MODEL slx_65e6816acb3b
CONFIG AbsTol = auto
CONFIG EnableMultiTasking = off
CONFIG FixedStep = 0.00001
CONFIG InitFcn = T = 0.0001;
VBUS = 12;

Wc = 10;
Ws = 50;
CONFIG MaxStep = auto
CONFIG MinStep = auto
CONFIG RelTol = 1e-3
CONFIG SampleTimeConstraint = Unconstrained
CONFIG SolverName = FixedStepAuto
CONFIG StartTime = 0.0
CONFIG StopTime = 5
BLOCK [SubSystem] Anti_Park
BLOCK [Fcn] Anti_Park/Fcn
  Expr = cos(u[1])*u[2]-sin(u[1])*u[3]
BLOCK [Fcn] Anti_Park/Fcn1
  Expr = sin(u[1])*u[2]+cos(u[1])*u[3]
BLOCK [Mux] Anti_Park/Mux1
  DisplayOption = bar
  Inputs = 3
BLOCK [Outport] Anti_Park/Ualpha
BLOCK [Outport] Anti_Park/Ubeta
  Port = 2
BLOCK [Inport] Anti_Park/Vd
  Port = 2
BLOCK [Inport] Anti_Park/Vq
BLOCK [Inport] Anti_Park/angle
  Port = 3
BLOCK [SubSystem] BPF滤波器Wc
BLOCK [Outport] BPF滤波器Wc/Out
BLOCK [TransferFcn] BPF滤波器Wc/Transfer Fcn1
  Denominator = [1 sqrt(2)*Wc Wc^2]
  Numerator = [Wc^2]
BLOCK [Inport] BPF滤波器Wc/Wc
BLOCK [SubSystem] BPF滤波器Wc1
  NameLocation = top
BLOCK [Outport] BPF滤波器Wc1/Out
BLOCK [TransferFcn] BPF滤波器Wc1/Transfer Fcn1
  Denominator = [1 sqrt(2)*Wc Wc^2]
  Numerator = [Wc^2]
BLOCK [Inport] BPF滤波器Wc1/Wc
BLOCK [SubSystem] BPF滤波器Wc2
  NameLocation = top
BLOCK [Outport] BPF滤波器Wc2/Out
BLOCK [TransferFcn] BPF滤波器Wc2/Transfer Fcn1
  Denominator = [1 sqrt(2)*Wc Wc^2]
  Numerator = [Wc^2]
BLOCK [Inport] BPF滤波器Wc2/Wc
BLOCK [SubSystem] BPF滤波器Ws
  NameLocation = top
BLOCK [Outport] BPF滤波器Ws/Out
BLOCK [TransferFcn] BPF滤波器Ws/Transfer Fcn1
  Denominator = [1 sqrt(2)*Ws Ws^2]
  Numerator = [Ws^2]
BLOCK [Inport] BPF滤波器Ws/Ws
BLOCK [SubSystem] CLARKE
BLOCK [Inport] CLARKE/A
BLOCK [Outport] CLARKE/Alpha
BLOCK [Inport] CLARKE/B
  Port = 2
BLOCK [Outport] CLARKE/Beta
  Port = 2
BLOCK [Inport] CLARKE/C
  Port = 3
BLOCK [Mux] CLARKE/Mux
  DisplayOption = bar
  Inputs = 3
BLOCK [Fcn] CLARKE/alpha
  Expr = (u(1)-0.5*(u(2)+u(3)))*2/3
BLOCK [Fcn] CLARKE/beta
  Expr = sqrt(3)/2*(u(2)-u(3))*2/3
BLOCK [Constant] Constant
BLOCK [Constant] Constant1
BLOCK [Constant] Constant2
BLOCK [Constant] Constant3
BLOCK [Constant] Constant4
  Value = 0
BLOCK [Constant] Constant5
BLOCK [Constant] Constant6
BLOCK [Reference] DC  REF=spsDCVoltageSourceLib/DC Voltage Source
  LibrarySourceBlock = sps_lib/Sources/DC Voltage Source
  NameLocation = right
  SourceBlock = spsDCVoltageSourceLib/DC Voltage Source
  SourceType = DC Voltage Source
BLOCK [Demux] Demux
  Outputs = 3
BLOCK [From] From
  GotoTag = Them
  NameLocation = right
BLOCK [From] From1
  GotoTag = Wm
  NameLocation = top
BLOCK [From] From2
  GotoTag = Them
  NameLocation = top
BLOCK [Goto] Goto
  GotoTag = Signal
BLOCK [Goto] Goto1
  GotoTag = Te
BLOCK [Goto] Goto2
  GotoTag = Them
BLOCK [Goto] Goto3
  GotoTag = Wm
BLOCK [Goto] Goto4
  GotoTag = Ialpha
BLOCK [Goto] Goto5
  GotoTag = Ibeta
BLOCK [SubSystem] Mux1
BLOCK [BusSelector] Mux1/Bus Selector
  OutputSignals = Stator current is_a (A),Stator current is_b (A),Stator current is_c (A)
BLOCK [BusSelector] Mux1/Bus Selector1
  OutputSignals = Rotor speed wm (rad/s),Rotor angle thetam (rad),Electromagnetic torque Te (N*m)
BLOCK [Outport] Mux1/Iabc
  Port = 3
BLOCK [Mux] Mux1/Mux
  DisplayOption = bar
  Inputs = 3
BLOCK [Outport] Mux1/Te
BLOCK [Outport] Mux1/Them
  Port = 2
BLOCK [Outport] Mux1/Wm
  Port = 4
BLOCK [Inport] Mux1/m
BLOCK [SubSystem] PARK
BLOCK [Inport] PARK/Alpha
BLOCK [Inport] PARK/Beta
  Port = 2
BLOCK [Outport] PARK/D
BLOCK [Mux] PARK/Mux
  DisplayOption = bar
  Inputs = 3
BLOCK [Outport] PARK/Q
  Port = 2
BLOCK [Inport] PARK/The
  Port = 3
BLOCK [Fcn] PARK/d
  Expr = u(1)*cos(u(3))+u(2)*sin(u(3))
BLOCK [Fcn] PARK/q
  Expr = -u(1)*sin(u(3))+u(2)*cos(u(3))
BLOCK [SubSystem] PI控制器
BLOCK [Inport] PI控制器/Error
BLOCK [Inport] PI控制器/Ki
  Port = 3
BLOCK [Inport] PI控制器/Kp
  Port = 2
BLOCK [Product] PI控制器/Product
BLOCK [Product] PI控制器/Product1
BLOCK [Sum] PI控制器/Sum
BLOCK [TransferFcn] PI控制器/Transfer Fcn
  Denominator = [1 0]
BLOCK [Outport] PI控制器/output
BLOCK [SubSystem] PI控制器D轴
  NameLocation = top
BLOCK [Inport] PI控制器D轴/Error
BLOCK [Inport] PI控制器D轴/Ki
  Port = 3
BLOCK [Inport] PI控制器D轴/Kp
  Port = 2
BLOCK [Product] PI控制器D轴/Product
BLOCK [Product] PI控制器D轴/Product1
BLOCK [Sum] PI控制器D轴/Sum
BLOCK [TransferFcn] PI控制器D轴/Transfer Fcn
  Denominator = [1 0]
BLOCK [Outport] PI控制器D轴/output
BLOCK [SubSystem] PI控制器Q轴
  NameLocation = top
BLOCK [Inport] PI控制器Q轴/Error
BLOCK [Inport] PI控制器Q轴/Ki
  Port = 3
BLOCK [Inport] PI控制器Q轴/Kp
  Port = 2
BLOCK [Product] PI控制器Q轴/Product
BLOCK [Product] PI控制器Q轴/Product1
BLOCK [Sum] PI控制器Q轴/Sum
BLOCK [TransferFcn] PI控制器Q轴/Transfer Fcn
  Denominator = [1 0]
BLOCK [Outport] PI控制器Q轴/output
BLOCK [SubSystem] PI控制器Velocity
BLOCK [Inport] PI控制器Velocity/Error
BLOCK [Inport] PI控制器Velocity/Ki
  Port = 3
BLOCK [Inport] PI控制器Velocity/Kp
  Port = 2
BLOCK [Product] PI控制器Velocity/Product
BLOCK [Product] PI控制器Velocity/Product1
BLOCK [Sum] PI控制器Velocity/Sum
BLOCK [TransferFcn] PI控制器Velocity/Transfer Fcn
  Denominator = [1 0]
BLOCK [Outport] PI控制器Velocity/output
BLOCK [SubSystem] PLL锁相环
BLOCK [Inport] PLL锁相环/Error
BLOCK [Inport] PLL锁相环/Ki
  Port = 3
BLOCK [Inport] PLL锁相环/Kp
  Port = 2
BLOCK [Product] PLL锁相环/Product
BLOCK [Product] PLL锁相环/Product1
BLOCK [Sum] PLL锁相环/Sum
BLOCK [TransferFcn] PLL锁相环/Transfer Fcn
  Denominator = [1 0]
BLOCK [TransferFcn] PLL锁相环/Transfer Fcn2
  Denominator = [1 0]
BLOCK [Outport] PLL锁相环/outRad
  Port = 2
BLOCK [Outport] PLL锁相环/outWe
BLOCK [Reference] Permanent Magnet Synchronous Machine1  REF=spsPermanentMagnetSynchronousMachineLib/Permanent Magnet
Synchronous Machine
  SourceBlock = spsPermanentMagnetSynchronousMachineLib/Permanent Magnet
Synchronous Machine
  SourceType = Permanent Magnet Synchronous Machine
BLOCK [SubSystem] SVPWM
BLOCK [CCaller] SVPWM/C Caller
  FunctionName = SVPWM
  PortSpecificationStruct = %)30     .    8 H   8    (     @         %    "     8    !     0         %  0 "0    $    _    07)G3F%M90  4&]R=$YA;64 4V-O<&4     26YD97@     5'EP90      4VEZ90      27-';&]B86P   X    P    !@    @    $          4    (     0    0    !         !  ! !60E53#@   #     &    "     0         !0    @    !    !     $         $  $ %9"55,.    .     8    (    !          %    "     $    %     0         0    !0...<+3154ch>
BLOCK [Constant] SVPWM/Constant2
  Value = VBUS
BLOCK [DataTypeConversion] SVPWM/Data Type Conversion
  OutDataTypeStr = double
  RndMeth = Floor
  SaturateOnIntegerOverflow = off
BLOCK [DataTypeConversion] SVPWM/Data Type Conversion1
  OutDataTypeStr = double
  RndMeth = Floor
  SaturateOnIntegerOverflow = off
BLOCK [DataTypeConversion] SVPWM/Data Type Conversion2
  OutDataTypeStr = double
  RndMeth = Floor
  SaturateOnIntegerOverflow = off
BLOCK [Logic] SVPWM/Logical Operator
  AllPortsSameDT = off
  Operator = NOT
  OutDataTypeStr = boolean
BLOCK [Logic] SVPWM/Logical Operator1
  AllPortsSameDT = off
  Operator = NOT
  OutDataTypeStr = boolean
BLOCK [Logic] SVPWM/Logical Operator2
  AllPortsSameDT = off
  Operator = NOT
  OutDataTypeStr = boolean
BLOCK [Mux] SVPWM/Mux
  DisplayOption = bar
  Inputs = 6
BLOCK [Reference] SVPWM/PWM Generator  REF=eePwmGenerator/PWM Generator
  LibrarySourceBlock = ee_sl_lib/Pulse Width
Modulation/PWM Generator
  SourceBlock = eePwmGenerator/PWM Generator
  SourceType = PWM Generator
BLOCK [Reference] SVPWM/PWM Generator1  REF=eePwmGenerator/PWM Generator
  LibrarySourceBlock = ee_sl_lib/Pulse Width
Modulation/PWM Generator
  SourceBlock = eePwmGenerator/PWM Generator
  SourceType = PWM Generator
BLOCK [Reference] SVPWM/PWM Generator2  REF=eePwmGenerator/PWM Generator
  LibrarySourceBlock = ee_sl_lib/Pulse Width
Modulation/PWM Generator
  SourceBlock = eePwmGenerator/PWM Generator
  SourceType = PWM Generator
BLOCK [Inport] SVPWM/Valpha
BLOCK [Inport] SVPWM/Vbeta
  Port = 2
BLOCK [ZeroOrderHold] SVPWM/Zero-Order Hold
  SampleTime = T
BLOCK [ZeroOrderHold] SVPWM/Zero-Order Hold1
  SampleTime = T
BLOCK [Outport] SVPWM/pulse
BLOCK [Scope] Scope
  ActiveDisplayYMaximum = 24.577855803107717
  ActiveDisplayYMinimum = -17.449565790069414
  Floating = off
  GraphicalSettings = {"AxesScalingProperties":{"AlignXAxis":"Center","AlignYAxis":"Center","AutoScaleXAxisLimits":false,"AxesScaling":"Manual","AxesScalingNumUpdates":10,"ExpandOnly":true,"ScaleAxesLimitsAtStop":false,"XAxisDataRange":100,"YAxisDataRange":80},"DisplayProperties":{"ColorOrder":["auto","auto","auto","auto","auto","auto","auto","auto","auto","auto","auto","auto","auto","auto","auto","auto","auto","auto",...<+2412ch>
  MultipleDisplayCache = [{"MaxYLimMag":24.577855803107717,"MaxYLimReal":24.577855803107717,"MinYLimMag":0,"MinYLimReal":-17.449565790069414,"PlotAsMagnitudePhase":false,"ShowGrid":true,"ShowLegend":true,"Title":"%<SignalLabel>","YLabel":""}]
  NameLocation = right
  NumInputPorts = 3
  ScopeFrameLocation = window
  ShowLegend = on
  WasSavedAsWebScope = on
  WindowPosition = [573.000000,323.000000,688.000000,501.000000,]
BLOCK [Step] Step
  After = 0
  NameLocation = left
  SampleTime = 0
  Time = 0
BLOCK [Sum] Sum
  Inputs = |+-
BLOCK [Sum] Sum1
  Inputs = |+-
BLOCK [Sum] Sum2
  Inputs = |+-
BLOCK [SubSystem] Theta_Signal
BLOCK [Sum] Theta_Signal/Add
  IconShape = rectangular
BLOCK [Constant] Theta_Signal/Constant3
BLOCK [Gain] Theta_Signal/Gain
  Gain = pi
BLOCK [Reference] Theta_Signal/Sawtooth Generator  REF=spsSawtoothGeneratorLib/Sawtooth
Generator
  LibrarySourceBlock = sps_lib/Sources/Signal Generator Sources/Sawtooth
Generator
  SourceBlock = spsSawtoothGeneratorLib/Sawtooth
Generator
  SourceType = Sawtooth Generator
BLOCK [Outport] Theta_Signal/angle
BLOCK [Reference] inverter  REF=spsUniversalBridgeLib/Universal Bridge
  LibrarySourceBlock = sps_lib/Power Electronics/Universal Bridge
  NameLocation = top
  SourceBlock = spsUniversalBridgeLib/Universal Bridge
  SourceType = Universal Bridge
BLOCK [Reference] powergui  REF=spspowerguiLib/powergui
  SourceBlock = spspowerguiLib/powergui
  SourceType = PSB option menu block
BLOCK [Step] 阶跃信号
  After = 72
  SampleTime = 1e-5
  Time = 3
LINE Anti_Park/Fcn1:1 -> Anti_Park/Ubeta:1
LINE Anti_Park/Fcn:1 -> Anti_Park/Ualpha:1
LINE Anti_Park/Mux1:1 -> Anti_Park/Fcn1:1
LINE Anti_Park/Mux1:1 -> Anti_Park/Fcn:1
LINE Anti_Park/Vd:1 -> Anti_Park/Mux1:2
LINE Anti_Park/Vq:1 -> Anti_Park/Mux1:3
LINE Anti_Park/angle:1 -> Anti_Park/Mux1:1
LINE Anti_Park:1 -> SVPWM:1
LINE Anti_Park:2 -> SVPWM:2
LINE BPF滤波器Wc/Transfer Fcn1:1 -> BPF滤波器Wc/Out:1
LINE BPF滤波器Wc/Wc:1 -> BPF滤波器Wc/Transfer Fcn1:1
LINE BPF滤波器Wc1/Transfer Fcn1:1 -> BPF滤波器Wc1/Out:1
LINE BPF滤波器Wc1/Wc:1 -> BPF滤波器Wc1/Transfer Fcn1:1
LINE BPF滤波器Wc1:1 -> CLARKE:2
LINE BPF滤波器Wc2/Transfer Fcn1:1 -> BPF滤波器Wc2/Out:1
LINE BPF滤波器Wc2/Wc:1 -> BPF滤波器Wc2/Transfer Fcn1:1
LINE BPF滤波器Wc2:1 -> CLARKE:1
LINE BPF滤波器Wc:1 -> CLARKE:3
LINE BPF滤波器Ws/Transfer Fcn1:1 -> BPF滤波器Ws/Out:1
LINE BPF滤波器Ws/Ws:1 -> BPF滤波器Ws/Transfer Fcn1:1
LINE BPF滤波器Ws:1 -> Sum2:2
LINE CLARKE/A:1 -> CLARKE/Mux:1
LINE CLARKE/B:1 -> CLARKE/Mux:2
LINE CLARKE/C:1 -> CLARKE/Mux:3
LINE CLARKE/Mux:1 -> CLARKE/alpha:1
LINE CLARKE/Mux:1 -> CLARKE/beta:1
LINE CLARKE/alpha:1 -> CLARKE/Alpha:1
LINE CLARKE/beta:1 -> CLARKE/Beta:1
LINE CLARKE:1 -> Goto4:1
LINE CLARKE:1 -> PARK:1
LINE CLARKE:2 -> Goto5:1
LINE CLARKE:2 -> PARK:2
LINE Constant1:1 -> PI控制器D轴:3
LINE Constant2:1 -> PI控制器Q轴:2
LINE Constant3:1 -> PI控制器Q轴:3
LINE Constant4:1 -> Sum1:1
LINE Constant5:1 -> PI控制器Velocity:2
LINE Constant6:1 -> PI控制器Velocity:3
LINE Constant:1 -> PI控制器D轴:2
LINE DC:lconn -> inverter:rconn
LINE DC:rconn -> inverter:rconn
LINE Demux:1 -> BPF滤波器Wc2:1
LINE Demux:2 -> BPF滤波器Wc1:1
LINE Demux:3 -> BPF滤波器Wc:1
LINE From1:1 -> BPF滤波器Ws:1
LINE From2:1 -> Anti_Park:3
LINE From:1 -> PARK:3
LINE Mux1/Bus Selector1:1 -> Mux1/Wm:1
LINE Mux1/Bus Selector1:2 -> Mux1/Them:1
LINE Mux1/Bus Selector1:3 -> Mux1/Te:1
LINE Mux1/Bus Selector:1 -> Mux1/Mux:1
LINE Mux1/Bus Selector:2 -> Mux1/Mux:2
LINE Mux1/Bus Selector:3 -> Mux1/Mux:3
LINE Mux1/Mux:1 -> Mux1/Iabc:1
LINE Mux1/m:1 -> Mux1/Bus Selector1:1
LINE Mux1/m:1 -> Mux1/Bus Selector:1
LINE Mux1:1 -> Goto1:1
LINE Mux1:1 -> Scope:1
LINE Mux1:2 -> Goto2:1
LINE Mux1:2 -> Scope:2
LINE Mux1:3 -> Demux:1
LINE Mux1:4 -> Goto3:1
LINE Mux1:4 -> Scope:3
LINE PARK/Alpha:1 -> PARK/Mux:1
LINE PARK/Beta:1 -> PARK/Mux:2
LINE PARK/Mux:1 -> PARK/d:1
LINE PARK/Mux:1 -> PARK/q:1
LINE PARK/The:1 -> PARK/Mux:3
LINE PARK/d:1 -> PARK/D:1
LINE PARK/q:1 -> PARK/Q:1
LINE PARK:1 -> Sum1:2
LINE PARK:2 -> Sum:2
LINE PI控制器/Error:1 -> PI控制器/Product1:1
LINE PI控制器/Error:1 -> PI控制器/Product:2
LINE PI控制器/Ki:1 -> PI控制器/Product1:2
LINE PI控制器/Kp:1 -> PI控制器/Product:1
LINE PI控制器/Product1:1 -> PI控制器/Transfer Fcn:1
LINE PI控制器/Product:1 -> PI控制器/Sum:1
LINE PI控制器/Sum:1 -> PI控制器/output:1
LINE PI控制器/Transfer Fcn:1 -> PI控制器/Sum:2
LINE PI控制器D轴/Error:1 -> PI控制器D轴/Product1:1
LINE PI控制器D轴/Error:1 -> PI控制器D轴/Product:2
LINE PI控制器D轴/Ki:1 -> PI控制器D轴/Product1:2
LINE PI控制器D轴/Kp:1 -> PI控制器D轴/Product:1
LINE PI控制器D轴/Product1:1 -> PI控制器D轴/Transfer Fcn:1
LINE PI控制器D轴/Product:1 -> PI控制器D轴/Sum:1
LINE PI控制器D轴/Sum:1 -> PI控制器D轴/output:1
LINE PI控制器D轴/Transfer Fcn:1 -> PI控制器D轴/Sum:2
LINE PI控制器D轴:1 -> Anti_Park:2
LINE PI控制器Q轴/Error:1 -> PI控制器Q轴/Product1:1
LINE PI控制器Q轴/Error:1 -> PI控制器Q轴/Product:2
LINE PI控制器Q轴/Ki:1 -> PI控制器Q轴/Product1:2
LINE PI控制器Q轴/Kp:1 -> PI控制器Q轴/Product:1
LINE PI控制器Q轴/Product1:1 -> PI控制器Q轴/Transfer Fcn:1
LINE PI控制器Q轴/Product:1 -> PI控制器Q轴/Sum:1
LINE PI控制器Q轴/Sum:1 -> PI控制器Q轴/output:1
LINE PI控制器Q轴/Transfer Fcn:1 -> PI控制器Q轴/Sum:2
LINE PI控制器Q轴:1 -> Anti_Park:1
LINE PI控制器Velocity/Error:1 -> PI控制器Velocity/Product1:1
LINE PI控制器Velocity/Error:1 -> PI控制器Velocity/Product:2
LINE PI控制器Velocity/Ki:1 -> PI控制器Velocity/Product1:2
LINE PI控制器Velocity/Kp:1 -> PI控制器Velocity/Product:1
LINE PI控制器Velocity/Product1:1 -> PI控制器Velocity/Transfer Fcn:1
LINE PI控制器Velocity/Product:1 -> PI控制器Velocity/Sum:1
LINE PI控制器Velocity/Sum:1 -> PI控制器Velocity/output:1
LINE PI控制器Velocity/Transfer Fcn:1 -> PI控制器Velocity/Sum:2
LINE PI控制器Velocity:1 -> Sum:1
LINE PLL锁相环/Error:1 -> PLL锁相环/Product1:1
LINE PLL锁相环/Error:1 -> PLL锁相环/Product:2
LINE PLL锁相环/Ki:1 -> PLL锁相环/Product1:2
LINE PLL锁相环/Kp:1 -> PLL锁相环/Product:1
LINE PLL锁相环/Product1:1 -> PLL锁相环/Transfer Fcn:1
LINE PLL锁相环/Product:1 -> PLL锁相环/Sum:1
LINE PLL锁相环/Sum:1 -> PLL锁相环/Transfer Fcn2:1
LINE PLL锁相环/Sum:1 -> PLL锁相环/outWe:1
LINE PLL锁相环/Transfer Fcn2:1 -> PLL锁相环/outRad:1
LINE PLL锁相环/Transfer Fcn:1 -> PLL锁相环/Sum:2
LINE Permanent Magnet Synchronous Machine1:1 -> Mux1:1
LINE Permanent Magnet Synchronous Machine1:lconn -> inverter:lconn
LINE Permanent Magnet Synchronous Machine1:lconn -> inverter:lconn
LINE SVPWM/C Caller:1 -> SVPWM/PWM Generator:1
LINE SVPWM/C Caller:2 -> SVPWM/PWM Generator1:1
LINE SVPWM/C Caller:3 -> SVPWM/PWM Generator2:1
LINE SVPWM/Constant2:1 -> SVPWM/C Caller:1
LINE SVPWM/Data Type Conversion1:1 -> SVPWM/Mux:4
LINE SVPWM/Data Type Conversion2:1 -> SVPWM/Mux:6
LINE SVPWM/Data Type Conversion:1 -> SVPWM/Mux:2
LINE SVPWM/Logical Operator1:1 -> SVPWM/Data Type Conversion1:1
LINE SVPWM/Logical Operator2:1 -> SVPWM/Data Type Conversion2:1
LINE SVPWM/Logical Operator:1 -> SVPWM/Data Type Conversion:1
LINE SVPWM/Mux:1 -> SVPWM/pulse:1
LINE SVPWM/PWM Generator1:1 -> SVPWM/Logical Operator1:1
LINE SVPWM/PWM Generator1:1 -> SVPWM/Mux:3
LINE SVPWM/PWM Generator2:1 -> SVPWM/Logical Operator2:1
LINE SVPWM/PWM Generator2:1 -> SVPWM/Mux:5
LINE SVPWM/PWM Generator:1 -> SVPWM/Logical Operator:1
LINE SVPWM/PWM Generator:1 -> SVPWM/Mux:1
LINE SVPWM/Valpha:1 -> SVPWM/Zero-Order Hold1:1
LINE SVPWM/Vbeta:1 -> SVPWM/Zero-Order Hold:1
LINE SVPWM/Zero-Order Hold1:1 -> SVPWM/C Caller:2
LINE SVPWM/Zero-Order Hold:1 -> SVPWM/C Caller:3
LINE SVPWM:1 -> inverter:1
LINE Step:1 -> Permanent Magnet Synchronous Machine1:1
LINE Sum1:1 -> PI控制器D轴:1
LINE Sum2:1 -> PI控制器Velocity:1
LINE Sum:1 -> PI控制器Q轴:1
LINE Theta_Signal/Add:1 -> Theta_Signal/Gain:1
LINE Theta_Signal/Constant3:1 -> Theta_Signal/Add:2
LINE Theta_Signal/Gain:1 -> Theta_Signal/angle:1
LINE Theta_Signal/Sawtooth Generator:1 -> Theta_Signal/Add:1
LINE Theta_Signal:1 -> Goto:1
LINE inverter:lconn -> Permanent Magnet Synchronous Machine1:lconn
LINE 阶跃信号:1 -> Sum2:1
